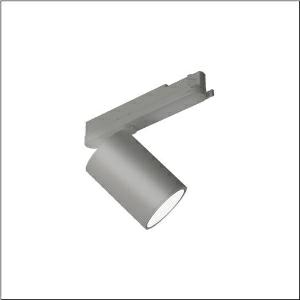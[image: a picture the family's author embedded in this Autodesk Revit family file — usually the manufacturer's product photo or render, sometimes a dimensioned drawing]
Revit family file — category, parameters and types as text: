
# Revit family: spot_31_51sf62mad4b
name_source: partatom
category: Lighting Fixtures
units: mm (PartAtom-declared; Revit-internal decimal feet)

## family parameters
Cut with Voids When Loaded = No
Host = Face
Light Source = No
Part Type = Normal
Room Calculation Point = No
Round Connector Dimension = Use Diameter
Shared = No

## types (1)
- --- (1 x LED, 5140 lm, 41.6 W, 4000K)
    Apparent Load = 42 VA
    CIE Flux Codes = 93 97 99 100 100
    Color Rendering = 90
    Color Temperature = 4000K
    Default Elevation = 1800 mm
    Description = Spot 31, directional spotlight, light control with lens, of PMMA, LED rated luminous flux: 4.930lm, light colour: 940, control gear: ECG Multilumen, with 3-phase adapter, mains connection: 220..240V, AC, 50/60Hz, of aluminium, metallic grey (RAL 9006), length: 213mm, diameter: 90mm, protection rating (complete): IP20, insulation class (complete): insulation class I (protective earthing), certification: CE, impact resistance: IK02, permissible ambient temperature for indoor applications: -20..+40°C, packaging unit: 1 piece
    Height = 175 mm
    Lamp = 1 x LED
    Lamp Light Flux = 5140 lm
    Lamp Power = 41.6 W
    Lamp count = 1
    Length = 90 mm
    Luminous efficacy = 124 lm/W
    Manufacturer = Siteco
    ModVariant = No
    Model = 51SF62MAD4B
    Mounting Place = Ceiling
    Mounting Type = Pendant
    Number of Poles = 1
    OnlyDefault = Yes
    Power Factor = 1
    Product Name = Spot 31
    Product group = directional spotlight
    ProductGroupID = 905
    Protection Class = Protection class I
    Protection Degree = IP 20
    RLX_Detail_Level = 1
    RLX_Emergency_Light_Flux = 0 lm
    RLX_Emergency_Type = 0
    RLX_Emergency_Type_DB = No
    RlxData = <blob elided: 20017 chars, md5=049f2ffb>
    Socket = socket
    Standby Power = 0 W
    System Light Flux = 5140 lm
    System Power = 42 W
    Type Comments = factory setting: luminous flux: 100 % | (ON | ON | ON | ON) | 1050 mA
    Type Image = l_1273725.jpg
    URL = http://relux.com
    VarID = @adj_096147
    Voltage = 0 V
    Weight = 0.00 kg
    Width = 0 mm  [stored 0 ft]

note: [stored X ft] marks values corroborated as IEEE doubles in the binary element streams (Revit-internal decimal feet)

## geometry (parser evidence)
native form markers: Blend x4, Sweep x10
no freeform markers — native parametric forms only
